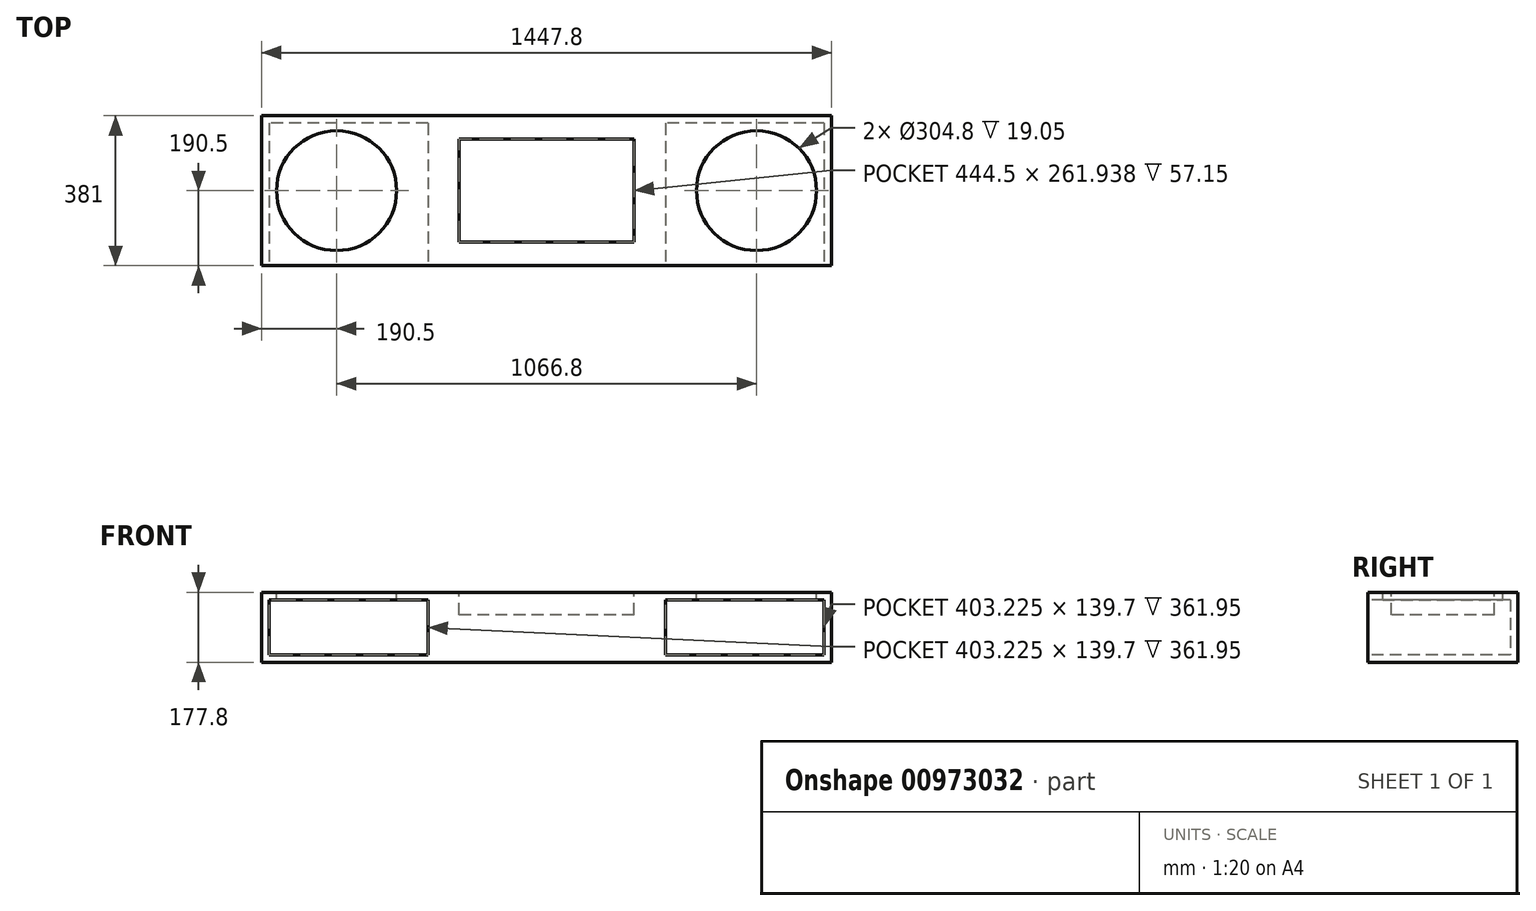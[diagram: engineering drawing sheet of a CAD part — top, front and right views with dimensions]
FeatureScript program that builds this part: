
annotation { "Feature Type Name" : "Feature", "Feature Type Description" : "" }
export const myFeature = defineFeature(function(context is Context, id is Id, definition is map)
    precondition{}
    {
        {
            var Q0;
            Q0=qCreatedBy(makeId("Top.planeOp"),FACE);
            var sketch = newSketch(context, id + "F0", { "sketchPlane" : qUnion([Q0])});
            skLineSegment(sketch, "E0.bottom", {"start": v(723.9, 190.5) * mm, "end": v(-723.9, 190.5) * mm});
            skLineSegment(sketch, "E0.top", {"start": v(723.9, -190.5) * mm, "end": v(-723.9, -190.5) * mm});
            skLineSegment(sketch, "E0.left", {"start": v(723.9, 190.5) * mm, "end": v(723.9, -190.5) * mm});
            skLineSegment(sketch, "E0.right", {"start": v(-723.9, 190.5) * mm, "end": v(-723.9, -190.5) * mm});
            skPoint(sketch, "E0.middle", {"position": v(0, 0) * mm});
            skSolve(sketch);
        }
        {
            var Q0;
            Q0 = qSketchRegion(id + "F0", true);
            extrude(context, id + "F1", {"entities" : qUnion([Q0]), "depth" : 177.8 * mm, "offsetDistance" : 25.4 * mm});
        }
        {
            var Q0;
            Q0=makeQuery(id+"F1.opExtrude","CAP_FACE",FACE,{"disambiguationData":[OSD([sQuery(id+"F0.wireOp",EDGE,"E0.bottom"),sQuery(id+"F0.wireOp",EDGE,"E0.top"),sQuery(id+"F0.wireOp",EDGE,"E0.left"),sQuery(id+"F0.wireOp",EDGE,"E0.right")])],"isStart":false});
            var sketch = newSketch(context, id + "F2", { "sketchPlane" : qUnion([Q0])});
            skCircle(sketch, "E1", {"center": v(-533.4, 0) * mm, "radius": 152.4 * mm});
            skCircle(sketch, "E2", {"center": v(533.4, 0) * mm, "radius": 152.4 * mm});
            skLineSegment(sketch, "E3.bottom", {"start": v(222.25, 130.97) * mm, "end": v(-222.25, 130.97) * mm});
            skLineSegment(sketch, "E3.top", {"start": v(222.25, -130.97) * mm, "end": v(-222.25, -130.97) * mm});
            skLineSegment(sketch, "E3.left", {"start": v(222.25, 130.97) * mm, "end": v(222.25, -130.97) * mm});
            skLineSegment(sketch, "E3.right", {"start": v(-222.25, 130.97) * mm, "end": v(-222.25, -130.97) * mm});
            skPoint(sketch, "E3.middle", {"position": v(0, 0) * mm});
            skSolve(sketch);
        }
        {
            var Q0;
            Q0=makeQuery(id+"F1.opExtrude","SWEPT_FACE",FACE,{"disambiguationData":[OSD([sQuery(id+"F0.wireOp",EDGE,"E0.top")])]});
            var sketch = newSketch(context, id + "F3", { "sketchPlane" : qUnion([Q0])});
            skPoint(sketch, "E4", {"position": v(-301.63, 177.8) * mm});
            skPoint(sketch, "E5", {"position": v(301.62, 0) * mm});
            skLineSegment(sketch, "E6.bottom", {"start": v(-301.63, 177.8) * mm, "end": v(301.62, 177.8) * mm});
            skLineSegment(sketch, "E6.top", {"start": v(-301.63, 0) * mm, "end": v(301.62, 0) * mm});
            skLineSegment(sketch, "E6.left", {"start": v(-301.63, 177.8) * mm, "end": v(-301.63, 0) * mm});
            skLineSegment(sketch, "E6.right", {"start": v(301.62, 177.8) * mm, "end": v(301.62, 0) * mm});
            skSolve(sketch);
        }
        {
            var Q0;
            Q0=makeQuery(id+"F1.opExtrude","SWEPT_FACE",FACE,{"disambiguationData":[OSD([sQuery(id+"F0.wireOp",EDGE,"E0.top")])]});
            shell(context, id + "F4", {"entities" : qUnion([Q0]), "thickness" : 19.05 * mm});
        }
        {
            var Q0;
            Q0=makeQuery(id+"F2.imprint","IMPRINT",FACE,{"disambiguationData":[TD([[makeQuery(id+"F2.imprint","IMPRINT",EDGE,{"derivedFrom":sQuery(id+"F2.wireOp",EDGE,"E1")}),1.0]])]});
            var Q1;
            Q1=makeQuery(id+"F2.imprint","IMPRINT",FACE,{"disambiguationData":[TD([[makeQuery(id+"F2.imprint","IMPRINT",EDGE,{"derivedFrom":sQuery(id+"F2.wireOp",EDGE,"E2")}),1.0]])]});
            extrude(context, id + "F5", {"entities" : qUnion([Q0, Q1]), "operationType" : NewBodyOperationType.REMOVE, "oppositeDirection" : true, "depth" : 25.4 * mm, "offsetDistance" : 25.4 * mm});
        }
        {
            var Q0;
            Q0 = qSketchRegion(id + "F3", true);
            extrude(context, id + "F6", {"entities" : qUnion([Q0]), "operationType" : NewBodyOperationType.ADD, "oppositeDirection" : true, "depth" : 381 * mm, "offsetDistance" : 25.4 * mm});
        }
        {
            var Q0;
            Q0=makeQuery(id+"F2.imprint","IMPRINT",FACE,{"disambiguationData":[TD([[makeQuery(id+"F2.imprint","IMPRINT",EDGE,{"derivedFrom":sQuery(id+"F2.wireOp",EDGE,"E3.bottom")}),1.0]])]});
            extrude(context, id + "F7", {"entities" : qUnion([Q0]), "operationType" : NewBodyOperationType.REMOVE, "oppositeDirection" : true, "depth" : 57.15 * mm, "offsetDistance" : 25.4 * mm});
        }
    });
